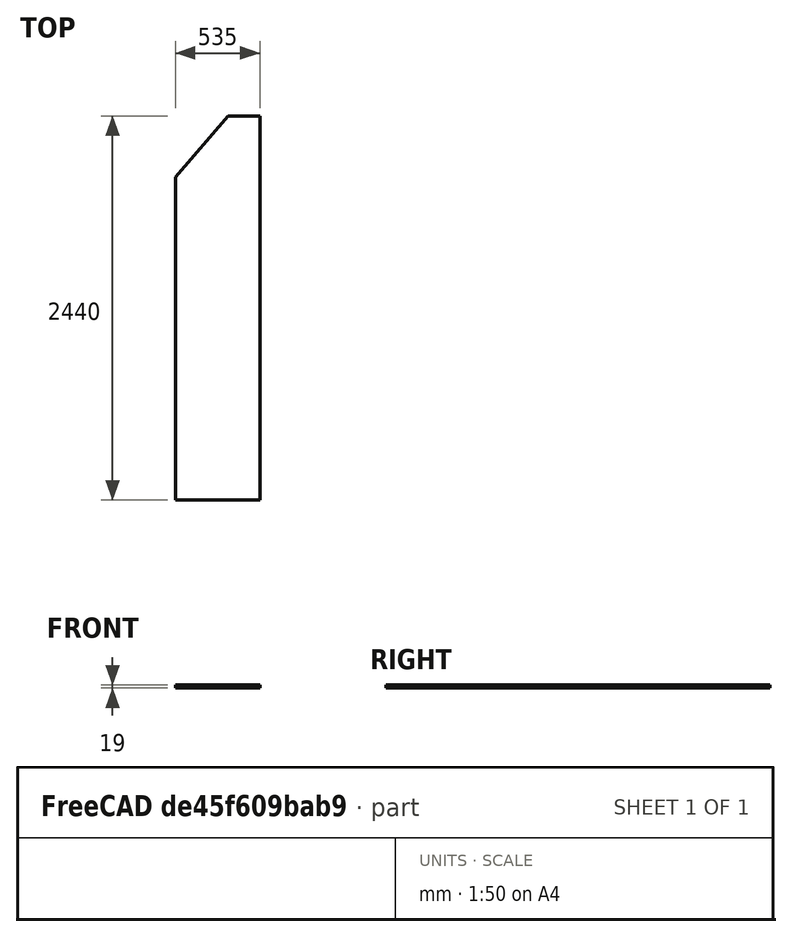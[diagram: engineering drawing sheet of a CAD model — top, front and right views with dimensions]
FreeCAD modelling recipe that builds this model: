
FCSTD DOCUMENT  (FreeCAD 1.0R39285 (Git))
Label: wardrobe_door_corpus00_jan
License: All rights reserved
LicenseURL: https://en.wikipedia.org/wiki/All_rights_reserved
objects: TechDraw::DrawViewDimension×7, PartDesign::CoordinateSystem×2, TechDraw::DrawProjGroupItem×2, Sketcher::SketchObject×1, PartDesign::Pad×1, PartDesign::Body×1, TechDraw::DrawSVGTemplate×1, TechDraw::DrawViewAnnotation×1, App::Part×1, TechDraw::DrawPage×1
note: 17 computed .brp shape members not serialized (recipe doc carries the construction recipe); baked Part::Feature solids carry a one-line shape summary decoded from their .brp
EXTERNAL_REF file=../../mastersheet.FCStd obj=Spreadsheet
EXTERNAL_REF file=../../mastersketch.FCStd obj=Sketch

FEATURE [Sketcher::SketchObject] Sketch
  ArcFitTolerance = 1e-06
  AttachmentSupport = -> [XY_Plane]
  FullyConstrained = true
  MakeInternals = false
  MapMode = 5
  expr: Constraints[0] = mastersketch#Sketch.Constraints.corpus00_door_height
  expr: Constraints[12] = mastersketch#Sketch.Constraints.alpha
  expr: Constraints[13] = mastersketch#Sketch.Constraints.corpus00_door_top
  expr: Constraints[5] = mastersheet#Spreadsheet.corpus_width - 5
  sketch-geometry (5):
    g0: LineSegment StartX=0 StartY=0 StartZ=0 EndX=0 EndY=2440 EndZ=0
    g1: LineSegment StartX=0 StartY=2440 StartZ=0 EndX=-202.892 EndY=2440 EndZ=0
    g2: LineSegment StartX=0 StartY=0 StartZ=0 EndX=-535 EndY=0 EndZ=0
    g3: LineSegment StartX=-535 StartY=0 StartZ=0 EndX=-535 EndY=2051.4 EndZ=0
    g4: LineSegment StartX=-535 StartY=2051.4 StartZ=0 EndX=-202.892 EndY=2440 EndZ=0
  constraints (14):
    c: Distance(g0) = 2440
    c: Coincident(g0,g-1)
    c: Vertical(g0)
    c: Coincident(g1,g0)
    c: Horizontal(g1)
    c: Distance(g2) = 535
    c: Coincident(g2,g0)
    c: PointOnObject(g2,g-1)
    c: Vertical(g3)
    c: Coincident(g4,g1)
    c: Coincident(g4,g3)
    c: Coincident(g3,g2)
    c: Angle(g3,g4) = 2.43442
    c: DistanceX(g1,g1) = 202.892
FEATURE [PartDesign::Pad] Pad
  Direction = (0,0,1)
  Length = 19
  Length2 = 10
  Profile = -> Sketch
  ReferenceAxis = -> Sketch [N_Axis]
  Refine = true
  Suppressed = false
  Type = 0
FEATURE [PartDesign::Body] Body  label="wardrobe_door_corpus00_jan"
  AllowCompound = false
  Group = -> [Sketch,Pad]
  Origin = -> Origin
  Tip = -> Pad
FEATURE [PartDesign::CoordinateSystem] LCS_right
  AttacherType = Attacher::AttachEngine3D
  AttachmentSupport = -> [Pad]
  MapMode = 7
  Placement = pos=(0,0,0) rot=(1,0,0;1.5708rad)
FEATURE [TechDraw::DrawSVGTemplate] Template  label="Vorlage"
  Height = 210
  Orientation = 1
  Template = <userpath>/scoop/apps/freecad/current/data/Mod/TechDraw/Templates/A4_Landscape_TD.svg
  Width = 297
FEATURE [TechDraw::DrawProjGroupItem] View  label="Oben"
  CoarseView = false
  Direction = (0,0,-1)
  Focus = 100
  HardHidden = false
  IsoCount = 0
  IsoHidden = false
  IsoVisible = false
  LockPosition = false
  Perspective = false
  Rotation = 0
  RotationVector = (1,0,0)
  Scale = 0.1
  ScaleType = 2
  ScrubCount = 1
  SeamHidden = false
  SeamVisible = false
  SmoothHidden = false
  SmoothVisible = true
  Source = -> [Body]
  Type = 0
  X = 142.185
  XDirection = (1e-16,-1,0)
  Y = 151.82
FEATURE [TechDraw::DrawProjGroupItem] View001  label="Seite"
  CoarseView = false
  Direction = (-1,-1e-16,0)
  Focus = 100
  HardHidden = false
  IsoCount = 0
  IsoHidden = false
  IsoVisible = false
  LockPosition = false
  Perspective = false
  Rotation = 0
  RotationVector = (1,0,0)
  Scale = 0.1
  ScaleType = 2
  ScrubCount = 1
  SeamHidden = false
  SeamVisible = false
  SmoothHidden = false
  SmoothVisible = true
  Source = -> [Body]
  Type = 0
  X = 143.628
  XDirection = (1e-16,-1,0)
  Y = 90.5756
FEATURE [TechDraw::DrawViewDimension] Dimension  label="Maß"
  AngleOverride = false
  Arbitrary = false
  ArbitraryTolerances = false
  BoxCorners = (2) [(-122,-26.75,0),(122,26.75,0)]
  EqualTolerance = true
  ExtensionAngle = 0
  FormatSpec = %.2w
  FormatSpecOverTolerance = %+.2w
  FormatSpecUnderTolerance = %+.2w
  Inverted = false
  LineAngle = 0
  LockPosition = false
  MeasureType = 1
  OverTolerance = 0
  References2D = -> [View]
  Rotation = 0
  ScaleType = 0
  TheoreticalExact = false
  Type = 0
  UnderTolerance = 0
  X = 129.212
  Y = 0
FEATURE [TechDraw::DrawViewDimension] Dimension001  label="Maß001"
  AngleOverride = false
  Arbitrary = false
  ArbitraryTolerances = false
  BoxCorners = (2) [(-122,-26.75,0),(122,26.75,0)]
  EqualTolerance = true
  ExtensionAngle = 0
  FormatSpec = %.2w
  FormatSpecOverTolerance = %+.2w
  FormatSpecUnderTolerance = %+.2w
  Inverted = false
  LineAngle = 0
  LockPosition = false
  MeasureType = 1
  OverTolerance = 0
  References2D = -> [View]
  Rotation = 0
  ScaleType = 0
  TheoreticalExact = false
  Type = 1
  UnderTolerance = 0
  X = 0
  Y = -32.8109
FEATURE [TechDraw::DrawViewDimension] Dimension002  label="Maß002"
  AngleOverride = false
  Arbitrary = false
  ArbitraryTolerances = false
  BoxCorners = (2) [(-122,-26.75,0),(122,26.75,0)]
  EqualTolerance = true
  ExtensionAngle = 0
  FormatSpec = %.2w
  FormatSpecOverTolerance = %+.2w
  FormatSpecUnderTolerance = %+.2w
  Inverted = false
  LineAngle = 0
  LockPosition = false
  MeasureType = 1
  OverTolerance = 0
  References2D = -> [View]
  Rotation = 0
  ScaleType = 0
  TheoreticalExact = false
  Type = 1
  UnderTolerance = 0
  X = 19.43
  Y = 40.4934
FEATURE [TechDraw::DrawViewDimension] Dimension003  label="Maß003"
  AngleOverride = false
  Arbitrary = false
  ArbitraryTolerances = false
  BoxCorners = (2) [(-122,-26.75,0),(122,26.75,0)]
  EqualTolerance = true
  ExtensionAngle = 0
  FormatSpec = %.1w
  FormatSpecOverTolerance = %+.2w
  FormatSpecUnderTolerance = %+.2w
  Inverted = false
  LineAngle = 0
  LockPosition = false
  MeasureType = 1
  OverTolerance = 0
  References2D = -> [View]
  Rotation = 0
  ScaleType = 0
  TheoreticalExact = false
  Type = 2
  UnderTolerance = 0
  X = -102.279
  Y = -16.6054
FEATURE [TechDraw::DrawViewDimension] Dimension004  label="Maß004"
  AngleOverride = false
  Arbitrary = false
  ArbitraryTolerances = false
  BoxCorners = (2) [(-122,-0.9,0),(122,0.9,0)]
  EqualTolerance = true
  ExtensionAngle = 0
  FormatSpec = %.2w
  FormatSpecOverTolerance = %+.2w
  FormatSpecUnderTolerance = %+.2w
  Inverted = false
  LineAngle = 0
  LockPosition = false
  MeasureType = 1
  OverTolerance = 0
  References2D = -> [View001]
  Rotation = 0
  ScaleType = 0
  TheoreticalExact = false
  Type = 0
  UnderTolerance = 0
  X = 124.097
  Y = -13.7815
FEATURE [TechDraw::DrawViewDimension] Dimension005  label="Maß005"
  AngleOverride = false
  Arbitrary = false
  ArbitraryTolerances = false
  BoxCorners = (2) [(-122,-26.75,0),(122,26.75,0)]
  EqualTolerance = true
  ExtensionAngle = 0
  FormatSpec = (%.1w)
  FormatSpecOverTolerance = %+.1w
  FormatSpecUnderTolerance = %+.1w
  Inverted = false
  LineAngle = 0
  LockPosition = false
  MeasureType = 1
  OverTolerance = 0
  References2D = -> [View]
  Rotation = 0
  ScaleType = 0
  TheoreticalExact = false
  Type = 6
  UnderTolerance = 0
  X = -75.6861
  Y = 12.9628
FEATURE [TechDraw::DrawViewAnnotation] Annotation  label="Beschriftung"
  Font = MS Shell Dlg 2
  LineSpace = 100
  LockPosition = false
  MaxWidth = -1
  Rotation = 0
  ScaleType = 0
  Text = Rev 01
  TextSize = 5
  TextStyle = 0
  X = 271.909
  Y = 62.045
FEATURE [PartDesign::CoordinateSystem] LCS_Origin
  AttacherType = Attacher::AttachEngine3D
  AttachmentSupport = -> [X_Axis001]
  MapMode = 2
FEATURE [App::Part] wardrobe_door_corpus00_jan  label="wardrobe_door_corpus00_jan001"
  DrawingName = wardrobe_door_corpus00_jan.FCStd
  Group = -> [LCS_Origin,LCS_right,Body]
  Origin = -> Origin001
  PartDescription = wardrobe_door_corpus00_jan
  PartID = wardrobe_door_corpus00_jan
FEATURE [TechDraw::DrawViewDimension] Dimension006  label="Maß006"
  AngleOverride = false
  Arbitrary = false
  ArbitraryTolerances = false
  BoxCorners = (2) [(-122,-26.75,0),(122,26.75,0)]
  EqualTolerance = true
  ExtensionAngle = 0
  FormatSpec = (%.1w)
  FormatSpecOverTolerance = %+.1w
  FormatSpecUnderTolerance = %+.1w
  Inverted = false
  LineAngle = 0
  LockPosition = false
  MeasureType = 1
  OverTolerance = 0
  References2D = -> [View]
  Rotation = 0
  ScaleType = 0
  TheoreticalExact = false
  Type = 0
  UnderTolerance = 0
  X = -112.05
  Y = 21.2372
FEATURE [TechDraw::DrawPage] Page  label="Drawing"
  KeepUpdated = true
  NextBalloonIndex = 1
  ProjectionType = 0
  Template = -> Template
  Views = -> [View,View001,Dimension,Dimension001,Dimension002,Dimension003,Dimension004,Dimension005,Annotation,Dimension006]
